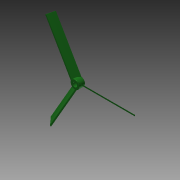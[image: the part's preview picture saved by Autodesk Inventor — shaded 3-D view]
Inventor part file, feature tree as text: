
AUTODESK INVENTOR PART (.ipt)
format: ipt  version: 2015 (Build 190159000, 159)  size: 125,440 bytes
history: native  units: mm
features: extrude x2, sketch x2, plane x1, fillet x1, pattern_circular x1
ambient origin geometry x8: Origin, YZ Plane, XZ Plane, XY Plane, X Axis, Y Axis, Z Axis, Center Point
bodies: Solid1 (feature_tree)
feature tree (7):
  extrude  "Extrusion1"  Depth=10.0mm
  plane  "Work Plane1"
  extrude  "Extrusion3"  Depth=40.0mm
  fillet  "Fillet2"  Radius=1.5mm
  pattern_circular  "Circular Pattern1"  [2 undecoded]
  sketch  "Sketch1"  dims[d1=127.0mm d4=10.0mm]
  sketch  "Sketch3"  dims[d5=7.0mm d6=0.0mm d13=40.0mm d15=1.5mm d16=2.0mm d17=58.5mm d18=0.0mm d19=0.0mm d24=0.25mm d26=30.0mm d27=360.0deg]
note: 2 required parameter values undecoded (feature->parameter linkage not recoverable at this tier; creation-order binding heuristic only, values carry confidence <= 0.55)
